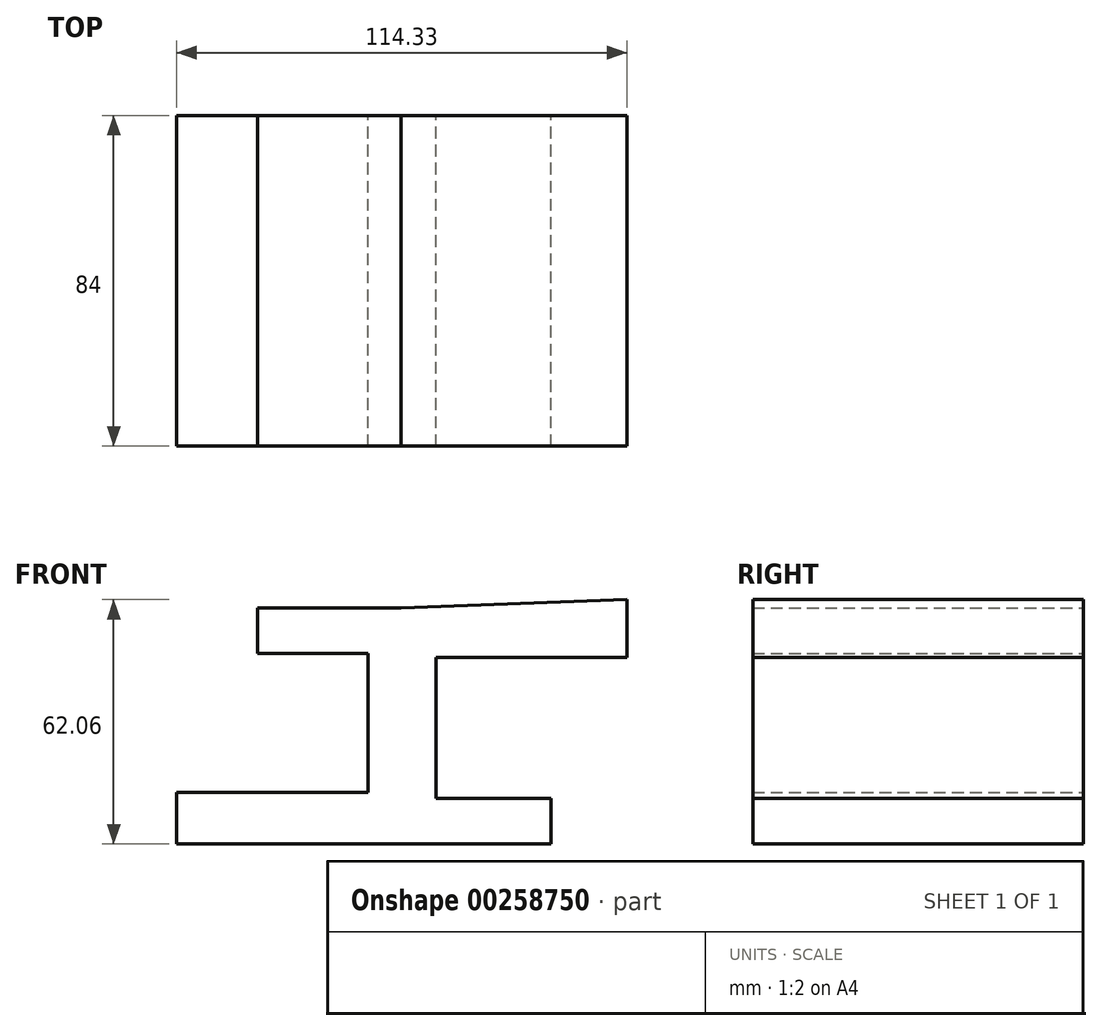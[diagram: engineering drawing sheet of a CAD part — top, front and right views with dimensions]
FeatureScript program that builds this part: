
annotation { "Feature Type Name" : "Feature", "Feature Type Description" : "" }
export const myFeature = defineFeature(function(context is Context, id is Id, definition is map)
    precondition{}
    {
        {
            var Q0;
            Q0=qCreatedBy(makeId("Front.planeOp"),FACE);
            var sketch = newSketch(context, id + "F0", { "sketchPlane" : qUnion([Q0])});
            skLineSegment(sketch, "E0", {"start": v(0, 32.7) * mm, "end": v(-36.4, 32.7) * mm});
            skLineSegment(sketch, "E1", {"start": v(-36.4, 32.7) * mm, "end": v(-36.4, 21.08) * mm});
            skLineSegment(sketch, "E2", {"start": v(-36.4, 21.08) * mm, "end": v(-8.34, 21.08) * mm});
            skLineSegment(sketch, "E3", {"start": v(-8.34, 21.08) * mm, "end": v(-8.34, -14.24) * mm});
            skLineSegment(sketch, "E4", {"start": v(-8.34, -14.24) * mm, "end": v(-56.97, -14.24) * mm});
            skLineSegment(sketch, "E5", {"start": v(-56.97, -14.24) * mm, "end": v(-56.97, -27.3) * mm});
            skLineSegment(sketch, "E6", {"start": v(-56.97, -27.3) * mm, "end": v(38.1, -27.3) * mm});
            skLineSegment(sketch, "E7", {"start": v(38.1, -27.3) * mm, "end": v(38.1, -15.7) * mm});
            skLineSegment(sketch, "E8", {"start": v(38.1, -15.7) * mm, "end": v(8.83, -15.7) * mm});
            skLineSegment(sketch, "E9", {"start": v(8.83, -15.7) * mm, "end": v(8.83, 20.11) * mm});
            skLineSegment(sketch, "E10", {"start": v(8.83, 20.11) * mm, "end": v(57.36, 20.11) * mm});
            skLineSegment(sketch, "E11", {"start": v(57.36, 20.11) * mm, "end": v(57.36, 34.76) * mm});
            skLineSegment(sketch, "E12", {"start": v(57.36, 34.76) * mm, "end": v(0, 32.7) * mm});
            skSolve(sketch);
        }
        {
            var Q0;
            Q0=makeQuery(id+"F0.imprint","IMPRINT",FACE,{"disambiguationData":[TD([[makeQuery(id+"F0.imprint","IMPRINT",EDGE,{"derivedFrom":sQuery(id+"F0.wireOp",EDGE,"E0")}),1.0]])]});
            extrude(context, id + "F1", {"entities" : qUnion([Q0]), "depth" : 84 * mm});
        }
    });
